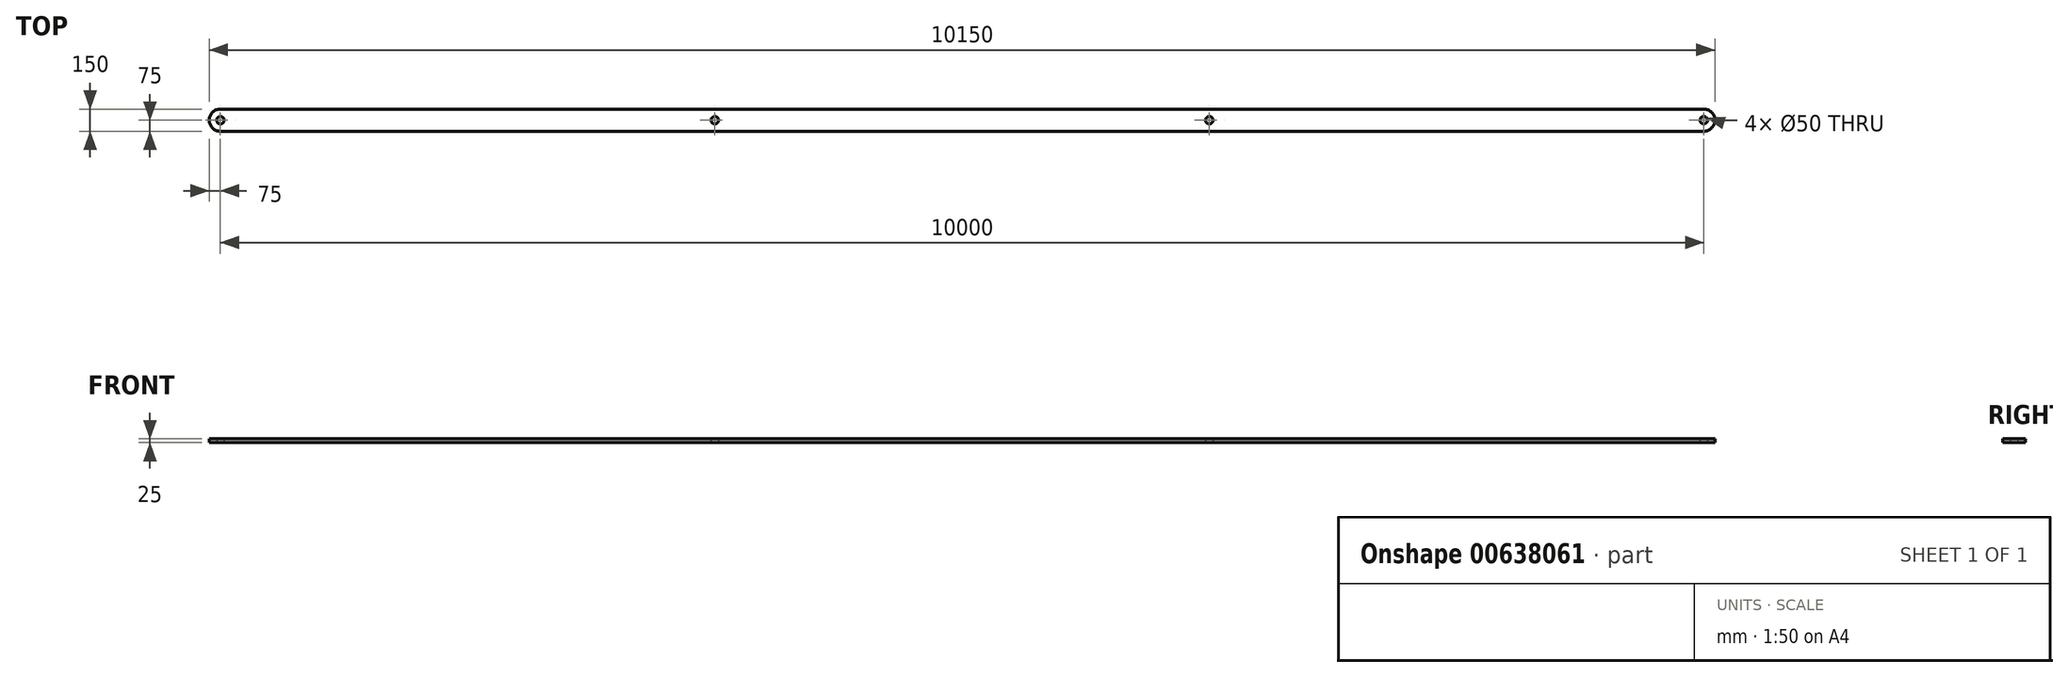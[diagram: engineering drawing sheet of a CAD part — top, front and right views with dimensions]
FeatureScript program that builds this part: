
annotation { "Feature Type Name" : "Feature", "Feature Type Description" : "" }
export const myFeature = defineFeature(function(context is Context, id is Id, definition is map)
    precondition{}
    {
        {
            var Q0;
            Q0=qCreatedBy(makeId("Top.planeOp"),FACE);
            var sketch = newSketch(context, id + "F0", { "sketchPlane" : qUnion([Q0])});
            skLineSegment(sketch, "E0", {"start": v(0, 0) * mm, "end": v(10000, 0) * mm});
            skLineSegment(sketch, "E1", {"start": v(10000, 0) * mm, "end": v(8333.33, 1500) * mm});
            skLineSegment(sketch, "E2", {"start": v(8333.33, 1500) * mm, "end": v(1666.67, 1500) * mm});
            skLineSegment(sketch, "E3", {"start": v(1666.67, 1500) * mm, "end": v(0, 0) * mm});
            skLineSegment(sketch, "E4", {"start": v(1666.67, 1500) * mm, "end": v(3333.33, 0) * mm});
            skLineSegment(sketch, "E5", {"start": v(3333.33, 0) * mm, "end": v(5000, 1500) * mm});
            skLineSegment(sketch, "E6", {"start": v(5000, 1500) * mm, "end": v(6666.67, 0) * mm});
            skLineSegment(sketch, "E7", {"start": v(6666.67, 0) * mm, "end": v(8333.33, 1500) * mm});
            skSolve(sketch);
        }
        {
            var Q0;
            Q0=qCreatedBy(makeId("Top.planeOp"),FACE);
            var sketch = newSketch(context, id + "F1", { "sketchPlane" : qUnion([Q0])});
            skLineSegment(sketch, "E8.0", {"start": v(0, 0) * mm, "end": v(10000, 0) * mm, "construction": true});
            skArc(sketch, "E9.0.startCap", {"start": v(0, -75) * mm, "mid": v(-75, 0) * mm, "end": v(0, 75) * mm});
            skArc(sketch, "E9.0.endCap", {"start": v(10000, 75) * mm, "mid": v(10075, 0) * mm, "end": v(10000, -75) * mm});
            skLineSegment(sketch, "E9.0.left", {"start": v(0, 75) * mm, "end": v(10000, 75) * mm});
            skLineSegment(sketch, "E9.0.right", {"start": v(0, -75) * mm, "end": v(10000, -75) * mm});
            skCircle(sketch, "E10", {"center": v(0, 0) * mm, "radius": 25 * mm});
            skPoint(sketch, "E11.0", {"position": v(3333.33, 0) * mm});
            skPoint(sketch, "E11.1", {"position": v(6666.67, 0) * mm});
            skCircle(sketch, "E12", {"center": v(3333.33, 0) * mm, "radius": 25 * mm});
            skCircle(sketch, "E13", {"center": v(6666.67, 0) * mm, "radius": 25 * mm});
            skCircle(sketch, "E14", {"center": v(10000, 0) * mm, "radius": 25 * mm});
            skSolve(sketch);
        }
        {
            var Q0;
            Q0 = qSketchRegion(id + "F1", true);
            extrude(context, id + "F2", {"entities" : qUnion([Q0]), "depth" : 25 * mm, "offsetDistance" : 25 * mm});
        }
    });
